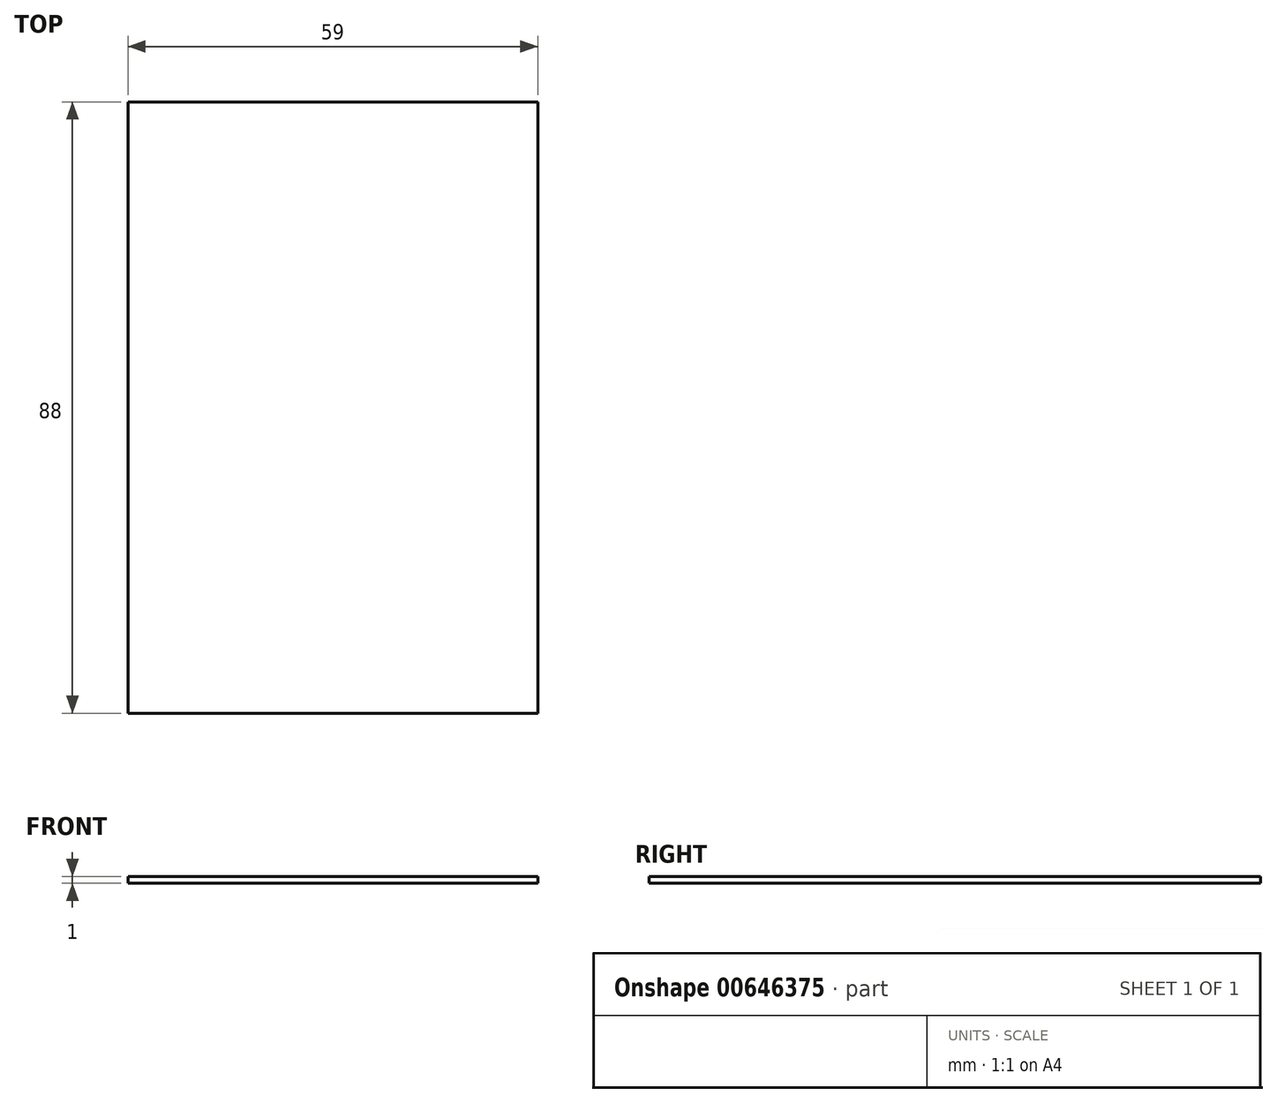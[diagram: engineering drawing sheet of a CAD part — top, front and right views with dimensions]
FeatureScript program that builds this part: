
annotation { "Feature Type Name" : "Feature", "Feature Type Description" : "" }
export const myFeature = defineFeature(function(context is Context, id is Id, definition is map)
    precondition{}
    {
        {
            var Q0;
            Q0=qCreatedBy(makeId("Top.planeOp"),FACE);
            var sketch = newSketch(context, id + "F0", { "sketchPlane" : qUnion([Q0])});
            skLineSegment(sketch, "E0.bottom", {"start": v(-8.56, 1.15) * mm, "end": v(50.44, 1.15) * mm});
            skLineSegment(sketch, "E0.top", {"start": v(-8.56, -86.85) * mm, "end": v(50.44, -86.85) * mm});
            skLineSegment(sketch, "E0.left", {"start": v(-8.56, 1.15) * mm, "end": v(-8.56, -86.85) * mm});
            skLineSegment(sketch, "E0.right", {"start": v(50.44, 1.15) * mm, "end": v(50.44, -86.85) * mm});
            skSolve(sketch);
        }
        {
            var Q0;
            Q0 = qSketchRegion(id + "F0", true);
            extrude(context, id + "F1", {"entities" : qUnion([Q0]), "depth" : 1 * mm, "offsetDistance" : 25 * mm});
        }
    });
